# Revit family: 1195x295_START Panel Backlit UGR19 - Copy (3) - Copy
name_source: partatom
category: Lighting Fixtures
revit_build: Autodesk Revit 2017 (Build: 20190507_1515(x64)
units: mm (PartAtom-declared; Revit-internal decimal feet)

## family parameters
Cut with Voids When Loaded = No
Host = Face
Light Source = Yes
OmniClass Number = 23.80.70.00
OmniClass Title = Lighting
Part Type = Normal
Room Calculation Point = No
Round Connector Dimension = Use Diameter
Shared = No

## types (1)
- 0042198
    -BOX_WIDTH_SYL = -40 mm
    -LUMDEPTH_SYL = -127 mm
    Apparent Load = 36 VA
    Assembly Code = D5020200
    AssetType = Fixed
    BOX_WIDTH_SYL = 40 mm  [stored 0.131234 ft]
    ClassificationName = Uniclass2015
    ClassificationValue = EF_70_80
    Color Filter = 16777215
    Cost = 0 $
    DEPTH_SYL = 598 mm
    Default Elevation = 1219 mm
    Dimming Lamp Color Temperature Shift = <None>
    DocumentationLiterature = http://www.sylvania-lighting.com
    ElectricShockClassification = Class II
    Emit Shape Visible in Rendering = No
    Emit from Circle Diameter = 610 mm
    HEIGHTBOTT_SYL = 7 mm  [stored 0.0229659 ft]
    HEIGHT_SYL = 33 mm  [stored 0.108268 ft]
    IfcExportType = IfcLightFixtureType
    ImpactProtectionIndex = IK03
    IngressProtection = IP40/20
    Keynote = 16500
    LUMDEPTH_SYL = 127 mm
    LUMWIDTH_SYL = 577 mm
    Lamp = LED
    LampColourRenderingIndex = 80
    LampColourTemperature = 3000 K
    LampMacAdamStep = 6
    LampNominalLuminous = 3600 lm
    LampsType = LED
    LuminousEfficacy = 100 lm/W
    MAINHEIGHT_SYL = 63 mm
    Manufacturer = Feilo Sylvania
    ManufacturerName = Feilo Sylvania
    Material = aluminium,steel housing, other diffuser
    Material_1_SYL = <By Category>
    Material_2_SYL = <By Category>
    Material_3_SYL = <By Category>
    Material_4_SYL = <By Category>
    Model = START Panel UGR19 1200x300 3600Lm 830 LILO
    ModelNumber = 0042198
    ModelReference = START Panel UGR19 1200x300 3600Lm 830 LILO
    Name = START Panel UGR19 1200x300 3600Lm 830 LILO
    NominalDepth = 295 mm  [stored 0.967848 ft]
    NominalHeight = 35 mm
    NominalLength = 1195 mm  [stored 3.9206 ft]
    Photometric Web File = 0042198.ies
    PowerConsumption = 36 W
    PowerFactor = 0.9
    TOP_DEPTH_SYL = 95 mm
    TOP_WIDTH_SYL = 265 mm  [stored 0.869423 ft]
    TOP__WIDTH_SYL = 545 mm
    Tilt Angle = -90.00°
    Type Image = <None>
    TypeName = START Panel UGR19 1200x300 3600Lm 830 LILO
    URL = http://www.sylvania-lighting.com\0042198
    Voltage = 0 V
    WIDTH_SYL = 148 mm
    Weight = 127.245 kg

note: [stored X ft] marks values corroborated as IEEE doubles in the binary element streams (Revit-internal decimal feet)

## geometry (parser evidence)
native form markers: Sweep x2
no freeform markers — native parametric forms only
